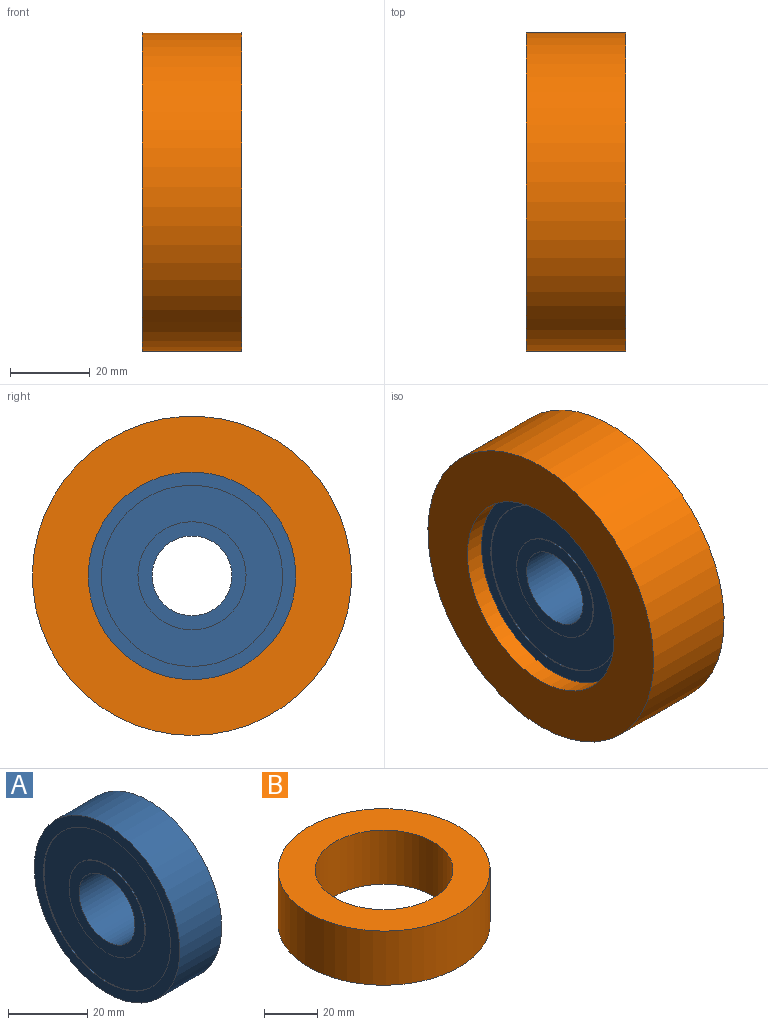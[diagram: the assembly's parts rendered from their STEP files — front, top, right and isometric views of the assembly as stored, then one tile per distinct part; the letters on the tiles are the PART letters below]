
ASSEMBLY  parts=2 mates=1
PART A: 12 faces, bbox 15x52x52 mm
  f0: plane 52x52mm, normal (-1,0,0), area 504.9mm2, adj f1,f11
  f1: cylinder r=22.7mm len=45.4mm, axis (-1,0,0), area 28.5mm2, adj f0,f2
  f2: plane 45.4x45.4mm, normal (-1,0,0), area 1042mm2, adj f1,f3
  f3: cylinder r=13.55mm len=27.1mm, axis (-1,0,0), area 17mm2, adj f2,f4
  f4: plane 27.1x27.1mm, normal (-1,0,0), area 262.6mm2, adj f3,f5
  f5: cylinder r=10mm len=20mm, axis (-1,0,0), area 942.5mm2, adj f4,f6
  f6: plane 27.1x27.1mm, normal (1,0,0), area 262.6mm2, adj f5,f7
  f7: cylinder r=13.55mm len=27.1mm, axis (-1,0,0), area 17mm2, adj f6,f8
  f8: plane 45.4x45.4mm, normal (1,0,0), area 1042mm2, adj f7,f9
  f9: cylinder r=22.7mm len=45.4mm, axis (-1,0,0), area 28.5mm2, adj f8,f10
  f10: plane 52x52mm, normal (1,0,0), area 504.9mm2, adj f9,f11
  f11: cylinder r=26mm len=52mm, axis (-1,0,0), area 2450.4mm2, adj f0,f10
PART B: 4 faces, bbox 80x80x25 mm
  f0: cylinder r=26mm len=52mm, axis (0,0,-1), area 4084.1mm2, adj f2,f3
  f1: cylinder r=40mm len=80mm, axis (0,0,-1), area 6283.2mm2, adj f2,f3
  f2: plane 80x80mm, normal (0,0,1), area 2902.8mm2, adj f0,f1
  f3: plane 80x80mm, normal (0,0,-1), area 2902.8mm2, adj f0,f1
PLACE A t=(-22.64,0.99,26.72)mm
PLACE B rot(axis=(0,1,0),90deg) t=(-35.14,16.33,-10.16)mm
MATE fastened A.f1 <-> B.f0  axis (-1,0,0) through (-22.64,0.99,26.72)mm
